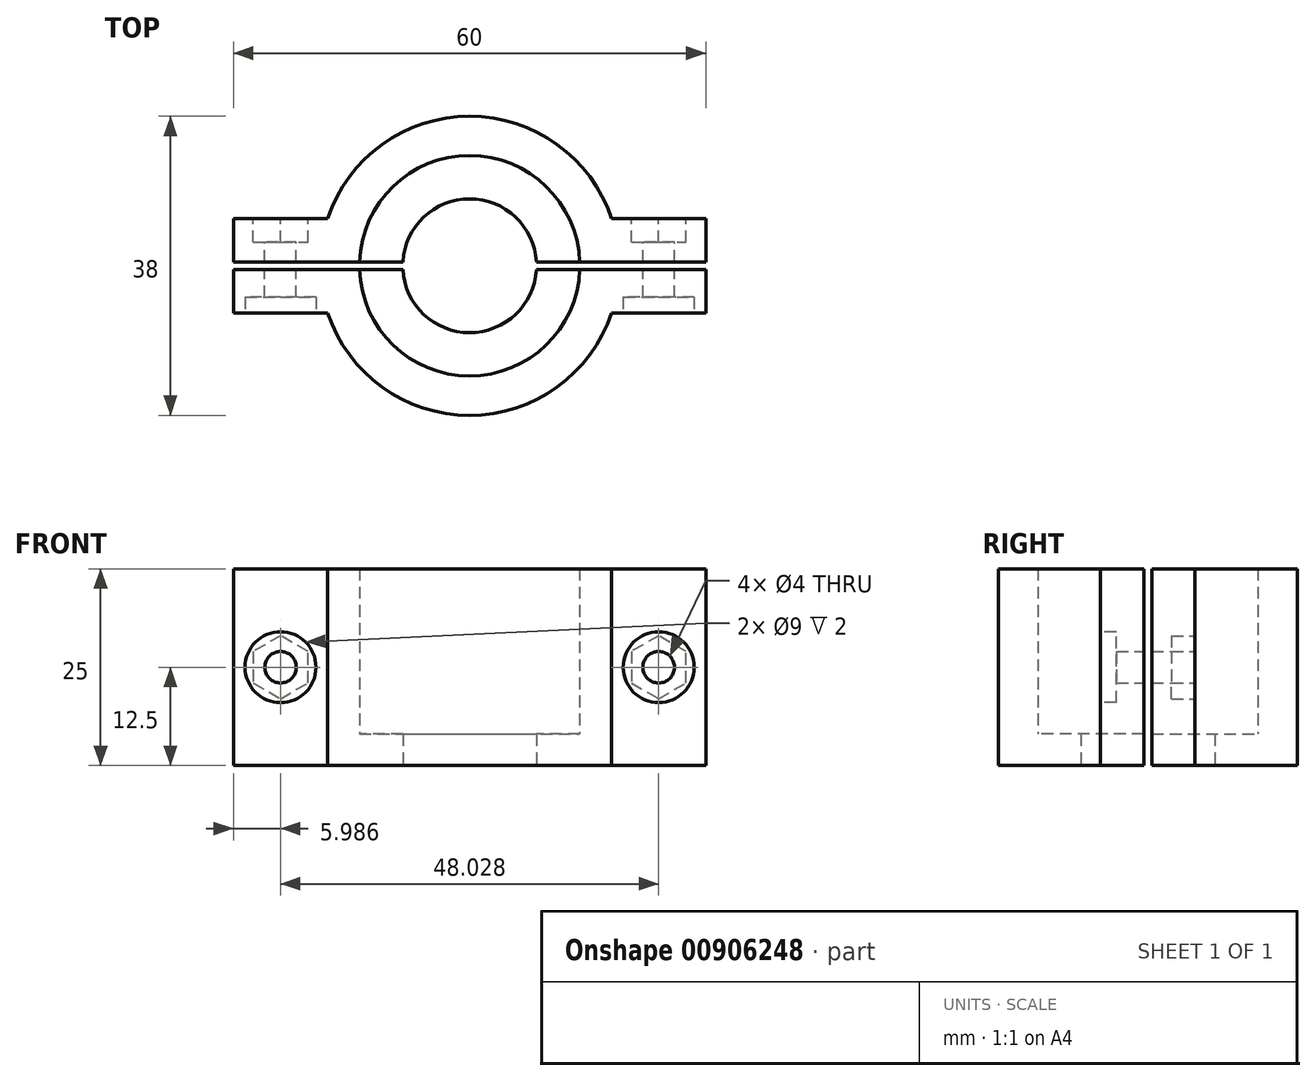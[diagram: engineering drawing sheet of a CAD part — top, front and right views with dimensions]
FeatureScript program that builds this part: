
annotation { "Feature Type Name" : "Feature", "Feature Type Description" : "" }
export const myFeature = defineFeature(function(context is Context, id is Id, definition is map)
    precondition{}
    {
        {
            var Q0;
            Q0=qCreatedBy(makeId("Top.planeOp"),FACE);
            var sketch = newSketch(context, id + "F0", { "sketchPlane" : qUnion([Q0])});
            skCircle(sketch, "E0", {"center": v(0, 0) * mm, "radius": 14 * mm});
            skArc(sketch, "E1", {"start": v(-18.03, -6) * mm, "mid": v(0, -19) * mm, "end": v(18.03, -6) * mm});
            skCircle(sketch, "E2", {"center": v(0, 0) * mm, "radius": 8.5 * mm});
            skCircle(sketch, "E3", {"center": v(0, 0) * mm, "radius": 8 * mm, "construction": true});
            skLineSegment(sketch, "E4.bottom", {"start": v(-30, -6) * mm, "end": v(-18.03, -6) * mm});
            skLineSegment(sketch, "E4.top", {"start": v(-30, 6) * mm, "end": v(-18.03, 6) * mm});
            skLineSegment(sketch, "E4.left", {"start": v(-30, -6) * mm, "end": v(-30, 6) * mm});
            skLineSegment(sketch, "E4.right", {"start": v(30, -6) * mm, "end": v(30, 6) * mm});
            skLineSegment(sketch, "E5.trimOffspring", {"start": v(18.03, -6) * mm, "end": v(30, -6) * mm});
            skLineSegment(sketch, "E6.trimOffspring", {"start": v(18.03, 6) * mm, "end": v(30, 6) * mm});
            skArc(sketch, "E7.trimOffspring", {"start": v(18.03, 6) * mm, "mid": v(0, 19) * mm, "end": v(-18.03, 6) * mm});
            skSolve(sketch);
        }
        {
            var Q0;
            Q0 = qSketchRegion(id + "F0", true);
            extrude(context, id + "F1", {"entities" : qUnion([Q0]), "depth" : 25 * mm, "offsetDistance" : 25 * mm});
        }
        {
            var Q0;
            Q0=makeQuery(id+"F0.imprint","IMPRINT",FACE,{"disambiguationData":[TD([[makeQuery(id+"F0.imprint","IMPRINT",EDGE,{"derivedFrom":sQuery(id+"F0.wireOp",EDGE,"E0")}),1.0]])]});
            extrude(context, id + "F2", {"entities" : qUnion([Q0]), "operationType" : NewBodyOperationType.ADD, "depth" : 4 * mm, "offsetDistance" : 25 * mm});
        }
        {
            var Q0;
            Q0=makeQuery(id+"F1.opExtrude","SWEPT_FACE",FACE,{"disambiguationData":[OSD([sQuery(id+"F0.wireOp",EDGE,"E6.trimOffspring")])]});
            var sketch = newSketch(context, id + "F3", { "sketchPlane" : qUnion([Q0])});
            skLineSegment(sketch, "E8", {"start": v(-24.01, 25) * mm, "end": v(-24.01, 0) * mm, "construction": true});
            skCircle(sketch, "E9", {"center": v(-24.01, 12.5) * mm, "radius": 2 * mm});
            skPoint(sketch, "E10.0", {"position": v(24.01, 25) * mm});
            skLineSegment(sketch, "E11", {"start": v(24.01, 25) * mm, "end": v(24.01, 0) * mm, "construction": true});
            skCircle(sketch, "E12", {"center": v(24.01, 12.5) * mm, "radius": 2 * mm});
            skCircle(sketch, "E13", {"center": v(24.01, 12.5) * mm, "radius": 4 * mm, "construction": true});
            skCircle(sketch, "E14", {"center": v(-24.01, 12.5) * mm, "radius": 4 * mm, "construction": true});
            skLineSegment(sketch, "E15.0", {"start": v(24.01, 8.5) * mm, "end": v(20.55, 10.5) * mm});
            skLineSegment(sketch, "E15.1", {"start": v(20.55, 10.5) * mm, "end": v(20.55, 14.5) * mm});
            skLineSegment(sketch, "E15.2", {"start": v(20.55, 14.5) * mm, "end": v(24.01, 16.5) * mm});
            skLineSegment(sketch, "E15.3", {"start": v(24.01, 16.5) * mm, "end": v(27.48, 14.5) * mm});
            skLineSegment(sketch, "E15.4", {"start": v(27.48, 14.5) * mm, "end": v(27.48, 10.5) * mm});
            skLineSegment(sketch, "E15.5", {"start": v(27.48, 10.5) * mm, "end": v(24.01, 8.5) * mm});
            skLineSegment(sketch, "E16.0", {"start": v(-24.01, 8.5) * mm, "end": v(-27.48, 10.5) * mm});
            skLineSegment(sketch, "E16.1", {"start": v(-27.48, 10.5) * mm, "end": v(-27.48, 14.5) * mm});
            skLineSegment(sketch, "E16.2", {"start": v(-27.48, 14.5) * mm, "end": v(-24.01, 16.5) * mm});
            skLineSegment(sketch, "E16.3", {"start": v(-24.01, 16.5) * mm, "end": v(-20.55, 14.5) * mm});
            skLineSegment(sketch, "E16.4", {"start": v(-20.55, 14.5) * mm, "end": v(-20.55, 10.5) * mm});
            skLineSegment(sketch, "E16.5", {"start": v(-20.55, 10.5) * mm, "end": v(-24.01, 8.5) * mm});
            skSolve(sketch);
        }
        {
            var Q0;
            Q0=makeQuery(id+"F3.imprint","IMPRINT",FACE,{"disambiguationData":[TD([[makeQuery(id+"F3.imprint","IMPRINT",EDGE,{"derivedFrom":sQuery(id+"F3.wireOp",EDGE,"E9")}),1.0]])]});
            var Q1;
            Q1=makeQuery(id+"F3.imprint","IMPRINT",FACE,{"disambiguationData":[TD([[makeQuery(id+"F3.imprint","IMPRINT",EDGE,{"derivedFrom":sQuery(id+"F3.wireOp",EDGE,"E12")}),1.0]])]});
            extrude(context, id + "F4", {"entities" : qUnion([Q0, Q1]), "operationType" : NewBodyOperationType.REMOVE, "oppositeDirection" : true, "depth" : 25 * mm, "offsetDistance" : 25 * mm});
        }
        {
            var Q0;
            Q0=makeQuery(id+"F3.imprint","IMPRINT",FACE,{"disambiguationData":[TD([[makeQuery(id+"F3.imprint","IMPRINT",EDGE,{"derivedFrom":sQuery(id+"F3.wireOp",EDGE,"E9")}),-1.0]])]});
            var Q1;
            Q1=makeQuery(id+"F3.imprint","IMPRINT",FACE,{"disambiguationData":[TD([[makeQuery(id+"F3.imprint","IMPRINT",EDGE,{"derivedFrom":sQuery(id+"F3.wireOp",EDGE,"E12")}),-1.0]])]});
            extrude(context, id + "F5", {"entities" : qUnion([Q0, Q1]), "operationType" : NewBodyOperationType.REMOVE, "oppositeDirection" : true, "depth" : 3 * mm, "offsetDistance" : 25 * mm});
        }
        {
            var Q0;
            Q0=makeQuery(id+"F1.opExtrude","SWEPT_FACE",FACE,{"disambiguationData":[OSD([sQuery(id+"F0.wireOp",EDGE,"E5.trimOffspring")])]});
            var sketch = newSketch(context, id + "F6", { "sketchPlane" : qUnion([Q0])});
            skCircle(sketch, "E17", {"center": v(24.01, 12.5) * mm, "radius": 4.5 * mm});
            skCircle(sketch, "E18.0", {"center": v(-24.01, 12.5) * mm, "radius": 2 * mm});
            skCircle(sketch, "E19", {"center": v(-24.01, 12.5) * mm, "radius": 4.5 * mm});
            skSolve(sketch);
        }
        {
            var Q0;
            Q0=makeQuery(id+"F6.imprint","IMPRINT",FACE,{"disambiguationData":[TD([[makeQuery(id+"F6.imprint","IMPRINT",EDGE,{"derivedFrom":sQuery(id+"F6.wireOp",EDGE,"E18.0")}),-1.0]])]});
            var Q1;
            Q1=makeQuery(id+"F6.imprint","IMPRINT",FACE,{"disambiguationData":[TD([[makeQuery(id+"F6.imprint","IMPRINT",EDGE,{"derivedFrom":sQuery(id+"F6.wireOp",EDGE,"E17")}),1.0]])]});
            extrude(context, id + "F7", {"entities" : qUnion([Q0, Q1]), "operationType" : NewBodyOperationType.REMOVE, "oppositeDirection" : true, "depth" : 2 * mm, "offsetDistance" : 25 * mm});
        }
        {
            var Q0;
            {var subQ0=sQuery(id+"F0.wireOp",EDGE,"E0");Q0=makeQuery(id+"F2.boolean.opBoolean","MERGE",FACE,{"derivedFrom":[makeQuery(id+"F1.opExtrude","CAP_FACE",FACE,{"disambiguationData":[OSD([subQ0,sQuery(id+"F0.wireOp",EDGE,"E1"),sQuery(id+"F0.wireOp",EDGE,"E4.bottom"),sQuery(id+"F0.wireOp",EDGE,"E4.top"),sQuery(id+"F0.wireOp",EDGE,"E4.left"),sQuery(id+"F0.wireOp",EDGE,"E4.right"),sQuery(id+"F0.wireOp",EDGE,"E5.trimOffspring"),sQuery(id+"F0.wireOp",EDGE,"E6.trimOffspring"),sQuery(id+"F0.wireOp",EDGE,"E7.trimOffspring")])],"isStart":true}),makeQuery(id+"F2.opExtrude","CAP_FACE",FACE,{"disambiguationData":[OSD([subQ0,sQuery(id+"F0.wireOp",EDGE,"E2")])],"isStart":true})]});}
            var sketch = newSketch(context, id + "F8", { "sketchPlane" : qUnion([Q0])});
            skLineSegment(sketch, "E20.0", {"start": v(-8.5, -0.5) * mm, "end": v(30, -0.5) * mm});
            skLineSegment(sketch, "E21.0", {"start": v(8.5, 0.5) * mm, "end": v(30, 0.5) * mm});
            skLineSegment(sketch, "E22.0", {"start": v(-30, -0.5) * mm, "end": v(-8.5, -0.5) * mm});
            skLineSegment(sketch, "E23.0", {"start": v(-30, 0.5) * mm, "end": v(8.5, 0.5) * mm});
            skSolve(sketch);
        }
        {
            var Q0;
            {var subQ0=sQuery(id+"F8.wireOp",EDGE,"E22.0");Q0=makeQuery(id+"F8.imprint","IMPRINT",FACE,{"disambiguationData":[TD([[makeQuery(id+"F8.imprint","IMPRINT",EDGE,{"derivedFrom":subQ0}),1.0]])]});}
            var Q1;
            {var subQ3=sQuery(id+"F8.wireOp",EDGE,"E21.0");Q1=makeQuery(id+"F8.imprint","IMPRINT",FACE,{"disambiguationData":[TD([[makeQuery(id+"F8.imprint","IMPRINT",EDGE,{"derivedFrom":subQ3}),-1.0]])]});}
            var Q2;
            {var subQ0=sQuery(id+"F8.wireOp",EDGE,"E20.0");var subQ1=makeQuery(id+"F2.opExtrude","CAP_EDGE",EDGE,{"disambiguationData":[OSD([sQuery(id+"F0.wireOp",EDGE,"E2")])],"isStart":true});var subQ2=makeQuery(id+"F8.imprint","INTERSECT",VERTEX,{"disambiguationData":[OD(0.0)],"derivedFrom":[subQ1,subQ0]});Q2=makeQuery(id+"F8.imprint","IMPRINT",FACE,{"disambiguationData":[TD([[makeQuery(id+"F8.imprint","IMPRINT",EDGE,{"disambiguationData":[TD([[subQ2,-1.0]])],"derivedFrom":subQ0}),1.0]])]});}
            extrude(context, id + "F9", {"entities" : qUnion([Q0, Q1, Q2]), "operationType" : NewBodyOperationType.REMOVE, "oppositeDirection" : true, "depth" : 30 * mm, "offsetDistance" : 25 * mm});
        }
    });
